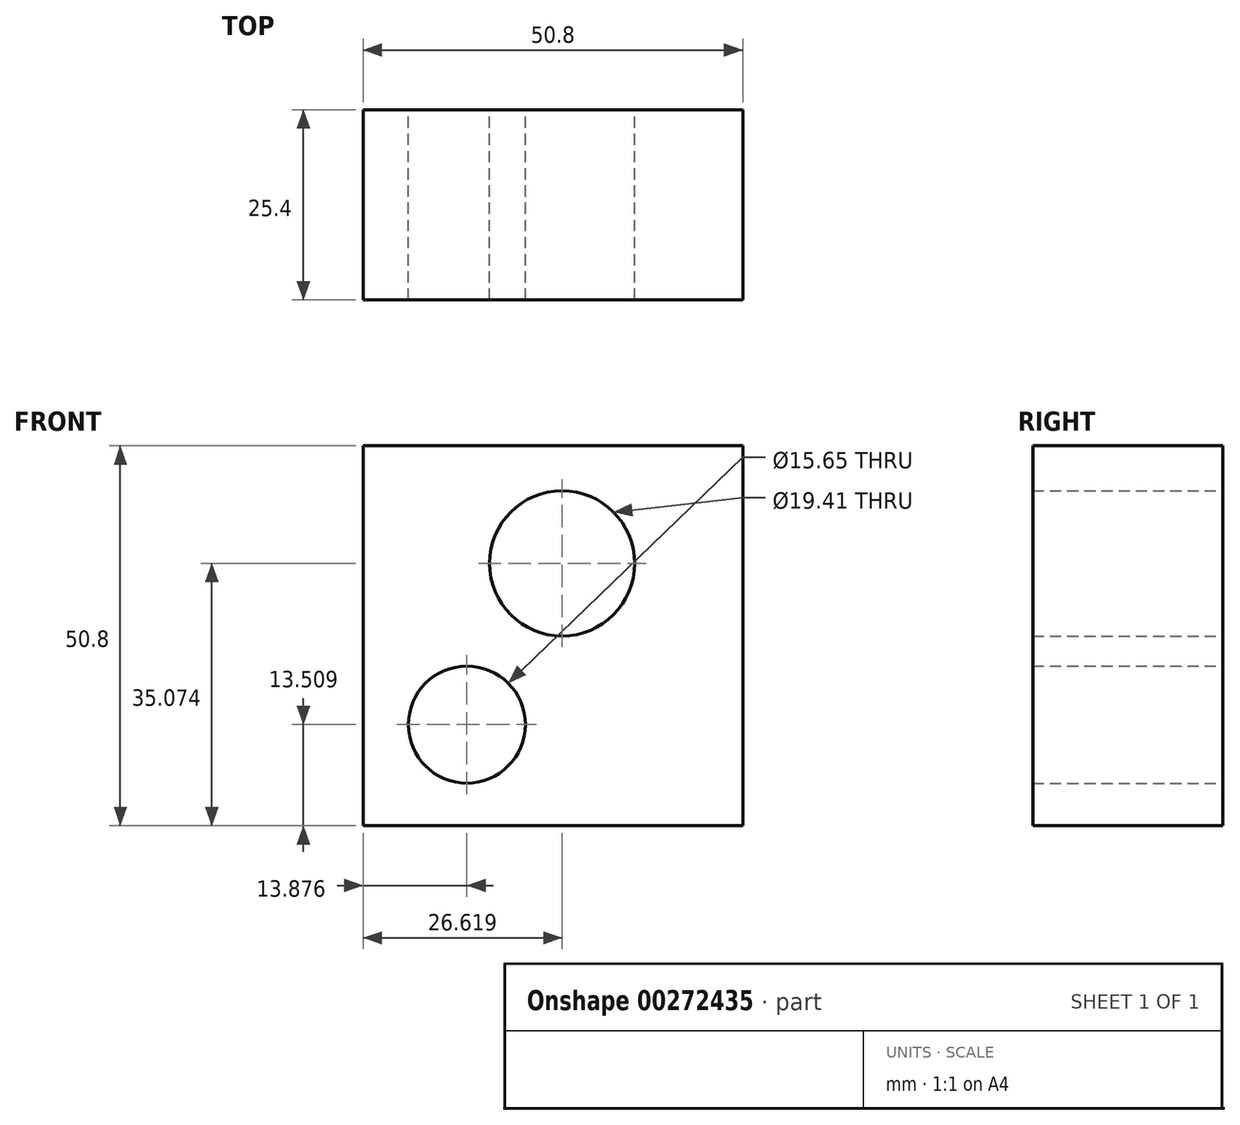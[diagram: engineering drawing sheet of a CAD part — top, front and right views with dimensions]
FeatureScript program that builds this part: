
annotation { "Feature Type Name" : "Feature", "Feature Type Description" : "" }
export const myFeature = defineFeature(function(context is Context, id is Id, definition is map)
    precondition{}
    {
        {
            var Q0;
            Q0=qCreatedBy(makeId("Front.planeOp"),FACE);
            var sketch = newSketch(context, id + "F0", { "sketchPlane" : qUnion([Q0])});
            skLineSegment(sketch, "E0.bottom", {"start": v(-54.8, 45.5) * mm, "end": v(-4, 45.5) * mm});
            skLineSegment(sketch, "E0.top", {"start": v(-54.8, -5.3) * mm, "end": v(-4, -5.3) * mm});
            skLineSegment(sketch, "E0.left", {"start": v(-54.8, 45.5) * mm, "end": v(-54.8, -5.3) * mm});
            skLineSegment(sketch, "E0.right", {"start": v(-4, 45.5) * mm, "end": v(-4, -5.3) * mm});
            skCircle(sketch, "E1", {"center": v(-40.92, 8.2) * mm, "radius": 7.82 * mm});
            skCircle(sketch, "E2", {"center": v(-28.18, 29.77) * mm, "radius": 9.7 * mm});
            skSolve(sketch);
        }
        {
            var Q0;
            Q0=makeQuery(id+"F0.imprint","IMPRINT",FACE,{"disambiguationData":[TD([[makeQuery(id+"F0.imprint","IMPRINT",EDGE,{"derivedFrom":sQuery(id+"F0.wireOp",EDGE,"E0.bottom")}),-1.0]])]});
            extrude(context, id + "F1", {"entities" : qUnion([Q0]), "depth" : 25.4 * mm});
        }
    });
